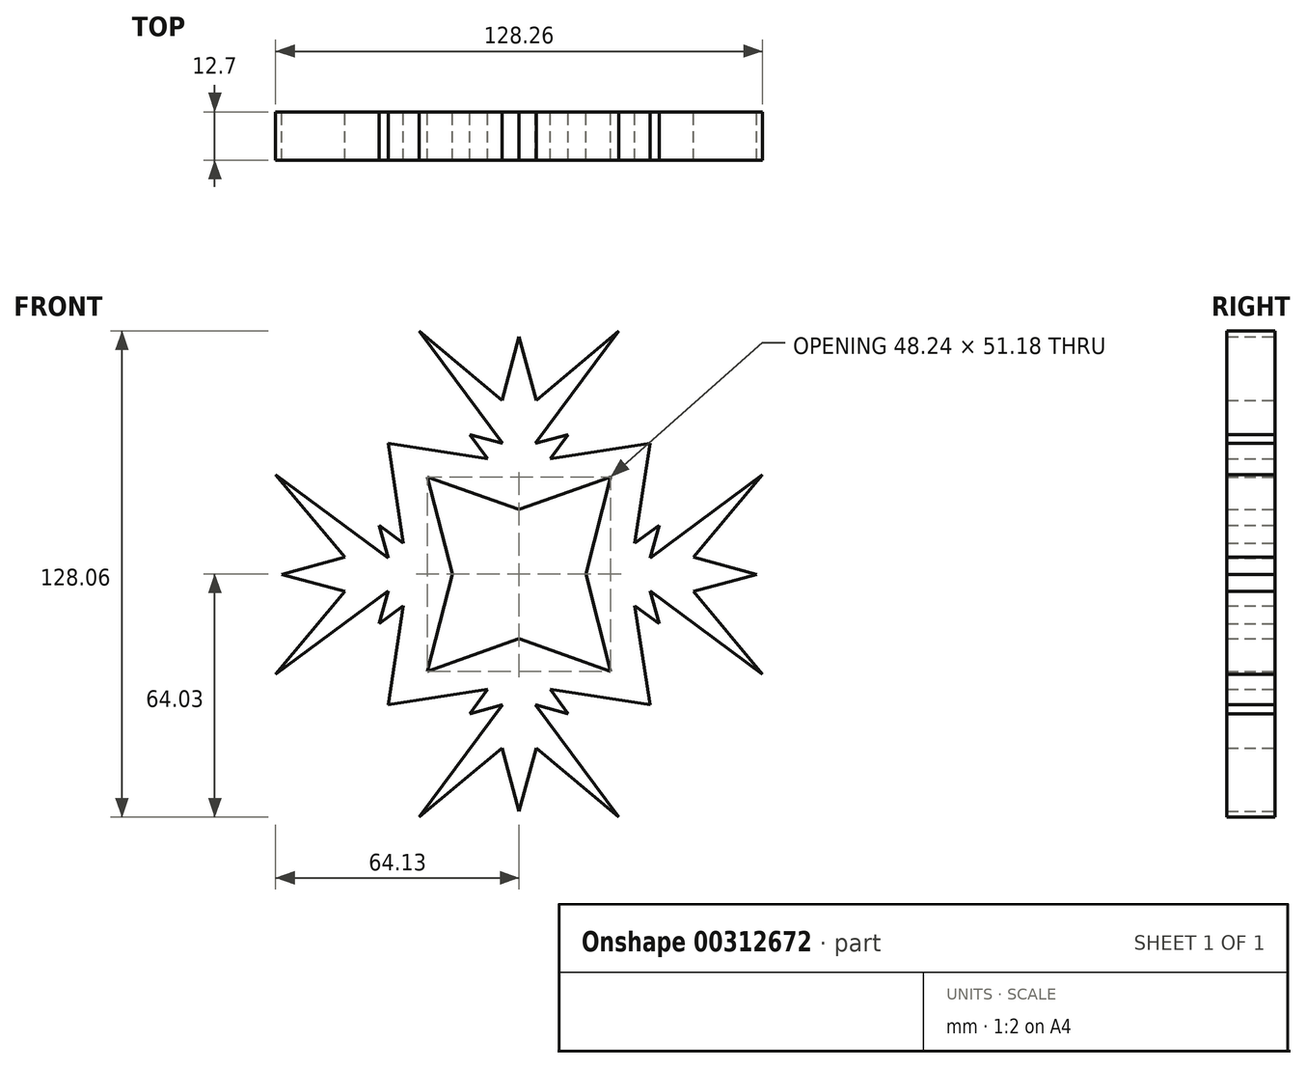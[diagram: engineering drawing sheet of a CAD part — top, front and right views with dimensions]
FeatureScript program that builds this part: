
annotation { "Feature Type Name" : "Feature", "Feature Type Description" : "" }
export const myFeature = defineFeature(function(context is Context, id is Id, definition is map)
    precondition{}
    {
        {
            var Q0;
            Q0=qCreatedBy(makeId("Front.planeOp"),FACE);
            var sketch = newSketch(context, id + "F0", { "sketchPlane" : qUnion([Q0])});
            skLineSegment(sketch, "E0", {"start": v(0, 62.46) * mm, "end": v(4.51, 45.8) * mm});
            skLineSegment(sketch, "E1", {"start": v(4.51, 45.8) * mm, "end": v(26.28, 64.03) * mm});
            skLineSegment(sketch, "E2", {"start": v(26.28, 64.03) * mm, "end": v(4.31, 34.42) * mm});
            skLineSegment(sketch, "E3", {"start": v(4.31, 34.42) * mm, "end": v(12.94, 36.77) * mm});
            skLineSegment(sketch, "E4", {"start": v(12.94, 36.77) * mm, "end": v(8.22, 30.4) * mm});
            skLineSegment(sketch, "E5", {"start": v(8.22, 30.4) * mm, "end": v(34.51, 34.42) * mm});
            skLineSegment(sketch, "E6.MirrorCS", {"start": v(0, 62.46) * mm, "end": v(-4.51, 45.8) * mm});
            skLineSegment(sketch, "E7.MirrorCS", {"start": v(-4.51, 45.8) * mm, "end": v(-26.28, 64.03) * mm});
            skLineSegment(sketch, "E8.MirrorCS", {"start": v(-26.28, 64.03) * mm, "end": v(-4.31, 34.42) * mm});
            skLineSegment(sketch, "E9.MirrorCS", {"start": v(-4.31, 34.42) * mm, "end": v(-12.94, 36.77) * mm});
            skLineSegment(sketch, "E10.MirrorCS", {"start": v(-12.94, 36.77) * mm, "end": v(-8.22, 30.4) * mm});
            skLineSegment(sketch, "E11.MirrorCS", {"start": v(-8.22, 30.4) * mm, "end": v(-34.51, 34.42) * mm});
            skLineSegment(sketch, "E12.MirrorCS", {"start": v(30.5, 8.12) * mm, "end": v(34.51, 34.42) * mm});
            skLineSegment(sketch, "E13.MirrorCS", {"start": v(36.87, 12.84) * mm, "end": v(30.5, 8.12) * mm});
            skLineSegment(sketch, "E14.MirrorCS", {"start": v(34.51, 4.22) * mm, "end": v(36.87, 12.84) * mm});
            skLineSegment(sketch, "E15.MirrorCS", {"start": v(64.13, 26.18) * mm, "end": v(34.51, 4.22) * mm});
            skLineSegment(sketch, "E16.MirrorCS", {"start": v(45.89, 4.41) * mm, "end": v(64.13, 26.18) * mm});
            skLineSegment(sketch, "E17.MirrorCS", {"start": v(62.56, -0.1) * mm, "end": v(45.89, 4.41) * mm});
            skLineSegment(sketch, "E18.MirrorCS", {"start": v(30.5, -8.32) * mm, "end": v(34.51, -34.61) * mm});
            skLineSegment(sketch, "E19.MirrorCS", {"start": v(36.87, -13.04) * mm, "end": v(30.5, -8.32) * mm});
            skLineSegment(sketch, "E20.MirrorCS", {"start": v(34.51, -4.41) * mm, "end": v(36.87, -13.04) * mm});
            skLineSegment(sketch, "E21.MirrorCS", {"start": v(64.13, -26.38) * mm, "end": v(34.51, -4.41) * mm});
            skLineSegment(sketch, "E22.MirrorCS", {"start": v(45.89, -4.6) * mm, "end": v(64.13, -26.38) * mm});
            skLineSegment(sketch, "E23.MirrorCS", {"start": v(62.56, -0.1) * mm, "end": v(45.89, -4.6) * mm});
            skLineSegment(sketch, "E24.MirrorCS", {"start": v(-8.22, -30.4) * mm, "end": v(-34.51, -34.42) * mm});
            skLineSegment(sketch, "E25.MirrorCS", {"start": v(-4.31, -34.42) * mm, "end": v(-12.94, -36.77) * mm});
            skLineSegment(sketch, "E26.MirrorCS", {"start": v(-12.94, -36.77) * mm, "end": v(-8.22, -30.4) * mm});
            skLineSegment(sketch, "E27.MirrorCS", {"start": v(-26.28, -64.03) * mm, "end": v(-4.31, -34.42) * mm});
            skLineSegment(sketch, "E28.MirrorCS", {"start": v(-4.51, -45.8) * mm, "end": v(-26.28, -64.03) * mm});
            skLineSegment(sketch, "E29.MirrorCS", {"start": v(0, -62.46) * mm, "end": v(-4.51, -45.8) * mm});
            skLineSegment(sketch, "E30.MirrorCS", {"start": v(0, -62.46) * mm, "end": v(4.51, -45.8) * mm});
            skLineSegment(sketch, "E31.MirrorCS", {"start": v(4.51, -45.8) * mm, "end": v(26.28, -64.03) * mm});
            skLineSegment(sketch, "E32.MirrorCS", {"start": v(26.28, -64.03) * mm, "end": v(4.31, -34.42) * mm});
            skLineSegment(sketch, "E33.MirrorCS", {"start": v(4.31, -34.42) * mm, "end": v(12.94, -36.77) * mm});
            skLineSegment(sketch, "E34.MirrorCS", {"start": v(8.22, -30.4) * mm, "end": v(34.51, -34.42) * mm});
            skLineSegment(sketch, "E35.MirrorCS", {"start": v(12.94, -36.77) * mm, "end": v(8.22, -30.4) * mm});
            skLineSegment(sketch, "E36.MirrorCS", {"start": v(-30.5, 8.12) * mm, "end": v(-34.51, 34.42) * mm});
            skLineSegment(sketch, "E37.MirrorCS", {"start": v(-36.87, 12.84) * mm, "end": v(-30.5, 8.12) * mm});
            skLineSegment(sketch, "E38.MirrorCS", {"start": v(-34.51, 4.22) * mm, "end": v(-36.87, 12.84) * mm});
            skLineSegment(sketch, "E39.MirrorCS", {"start": v(-64.13, 26.18) * mm, "end": v(-34.51, 4.22) * mm});
            skLineSegment(sketch, "E40.MirrorCS", {"start": v(-62.56, -0.1) * mm, "end": v(-45.89, 4.41) * mm});
            skLineSegment(sketch, "E41.MirrorCS", {"start": v(-62.56, -0.1) * mm, "end": v(-45.89, -4.6) * mm});
            skLineSegment(sketch, "E42.MirrorCS", {"start": v(-45.89, -4.6) * mm, "end": v(-64.13, -26.38) * mm});
            skLineSegment(sketch, "E43.MirrorCS", {"start": v(-64.13, -26.38) * mm, "end": v(-34.51, -4.41) * mm});
            skLineSegment(sketch, "E44.MirrorCS", {"start": v(-34.51, -4.41) * mm, "end": v(-36.87, -13.04) * mm});
            skLineSegment(sketch, "E45.MirrorCS", {"start": v(-36.87, -13.04) * mm, "end": v(-30.5, -8.32) * mm});
            skLineSegment(sketch, "E46.MirrorCS", {"start": v(-30.5, -8.32) * mm, "end": v(-34.51, -34.61) * mm});
            skLineSegment(sketch, "E47.MirrorCS", {"start": v(-45.89, 4.41) * mm, "end": v(-64.13, 26.18) * mm});
            skLineSegment(sketch, "E48", {"start": v(0, 17.04) * mm, "end": v(24.12, 25.6) * mm});
            skLineSegment(sketch, "E49", {"start": v(24.12, 25.6) * mm, "end": v(17.58, 0) * mm});
            skLineSegment(sketch, "E50.MirrorCS", {"start": v(24.12, -25.6) * mm, "end": v(17.58, 0) * mm});
            skLineSegment(sketch, "E51.MirrorCS", {"start": v(0, -17.04) * mm, "end": v(24.12, -25.6) * mm});
            skLineSegment(sketch, "E52.MirrorCS", {"start": v(0, 17.04) * mm, "end": v(-24.12, 25.6) * mm});
            skLineSegment(sketch, "E53.MirrorCS", {"start": v(-24.12, 25.6) * mm, "end": v(-17.58, 0) * mm});
            skLineSegment(sketch, "E54.MirrorCS", {"start": v(-24.12, -25.6) * mm, "end": v(-17.58, 0) * mm});
            skLineSegment(sketch, "E55.MirrorCS", {"start": v(0, -17.04) * mm, "end": v(-24.12, -25.6) * mm});
            skSolve(sketch);
        }
        {
            var Q0;
            Q0 = qSketchRegion(id + "F0", true);
            extrude(context, id + "F1", {"entities" : qUnion([Q0]), "depth" : 12.7 * mm, "offsetDistance" : 25.4 * mm});
        }
    });
